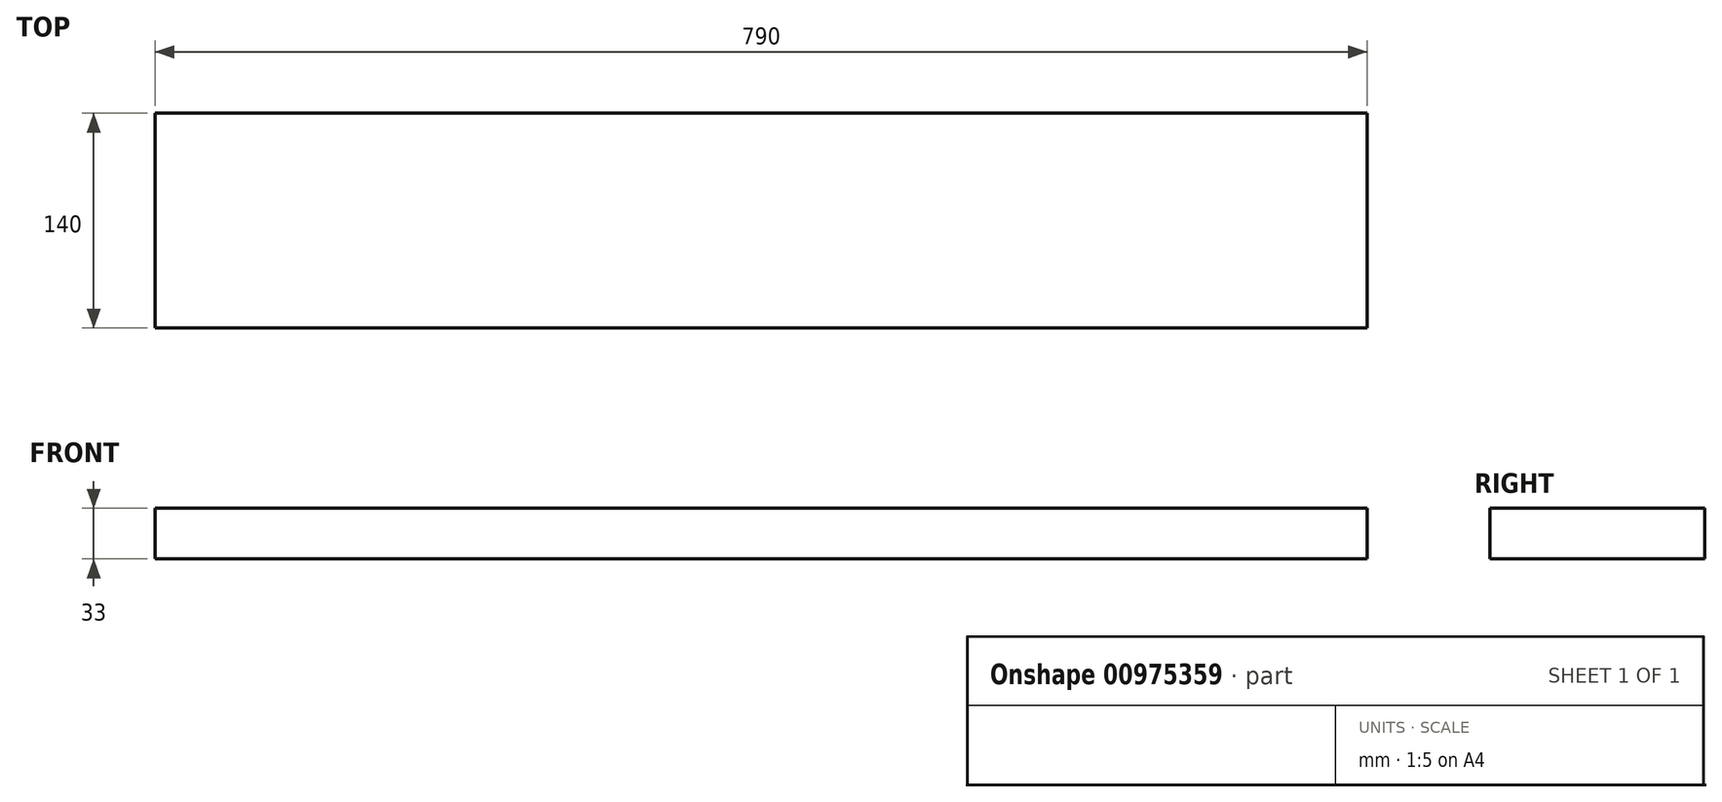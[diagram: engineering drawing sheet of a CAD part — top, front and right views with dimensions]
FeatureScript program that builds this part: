
annotation { "Feature Type Name" : "Feature", "Feature Type Description" : "" }
export const myFeature = defineFeature(function(context is Context, id is Id, definition is map)
    precondition{}
    {
        {
            var Q0;
            Q0=qCreatedBy(makeId("Top.planeOp"),FACE);
            var sketch = newSketch(context, id + "F0", { "sketchPlane" : qUnion([Q0])});
            skLineSegment(sketch, "E0.bottom", {"start": v(395, 70) * mm, "end": v(-395, 70) * mm});
            skLineSegment(sketch, "E0.top", {"start": v(395, -70) * mm, "end": v(-395, -70) * mm});
            skLineSegment(sketch, "E0.left", {"start": v(395, 70) * mm, "end": v(395, -70) * mm});
            skLineSegment(sketch, "E0.right", {"start": v(-395, 70) * mm, "end": v(-395, -70) * mm});
            skPoint(sketch, "E0.middle", {"position": v(0, 0) * mm});
            skSolve(sketch);
        }
        {
            var Q0;
            Q0=makeQuery(id+"F0.imprint","IMPRINT",FACE,{"disambiguationData":[TD([[makeQuery(id+"F0.imprint","IMPRINT",EDGE,{"derivedFrom":sQuery(id+"F0.wireOp",EDGE,"E0.bottom")}),1.0]])]});
            extrude(context, id + "F1", {"entities" : qUnion([Q0]), "endBound" : BoundingType.SYMMETRIC, "depth" : 33 * mm, "offsetDistance" : 25 * mm});
        }
    });
